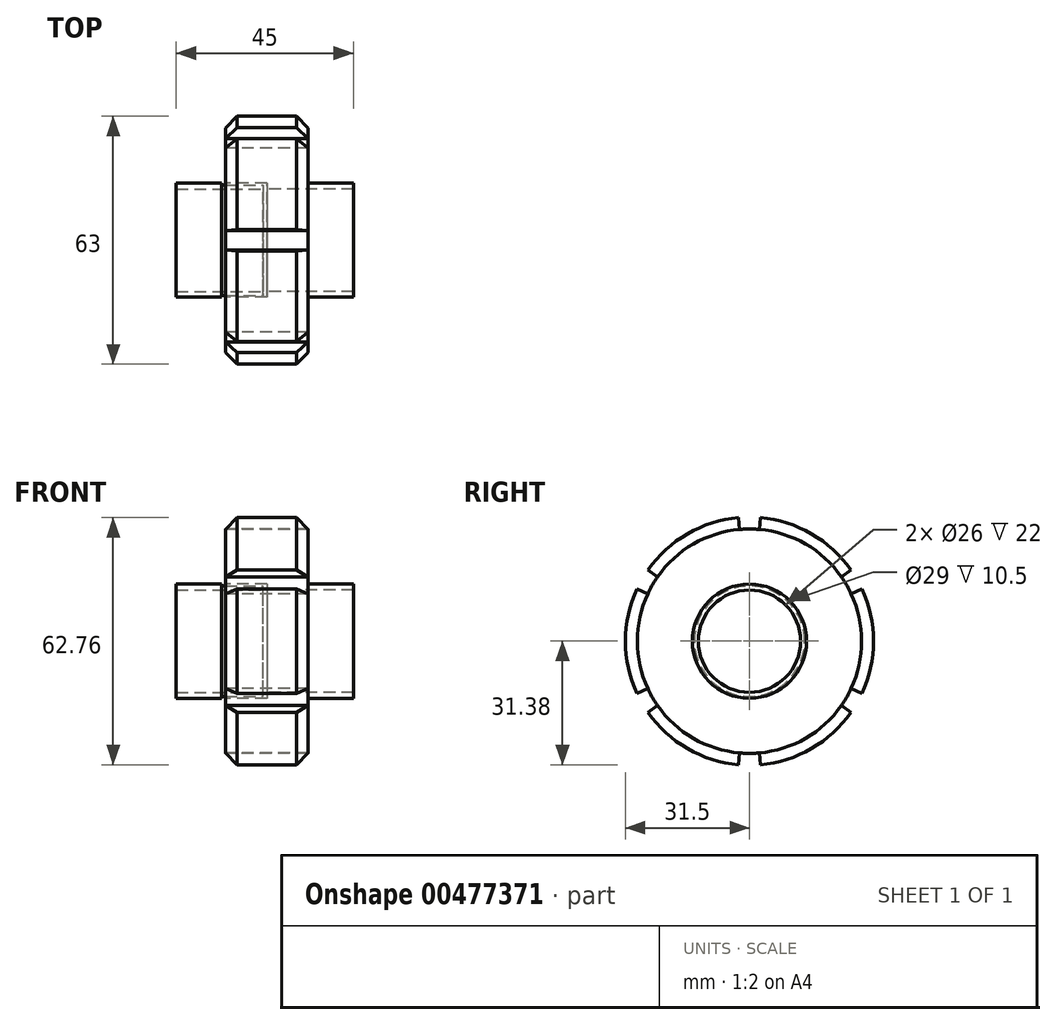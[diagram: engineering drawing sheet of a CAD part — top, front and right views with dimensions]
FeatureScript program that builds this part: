
annotation { "Feature Type Name" : "Feature", "Feature Type Description" : "" }
export const myFeature = defineFeature(function(context is Context, id is Id, definition is map)
    precondition{}
    {
        {
            var Q0;
            Q0=qCreatedBy(makeId("Front.planeOp"),FACE);
            var sketch = newSketch(context, id + "F0", { "sketchPlane" : qUnion([Q0])});
            skLineSegment(sketch, "E0", {"start": v(0, 0) * mm, "end": v(45.26, 0) * mm, "construction": true});
            skLineSegment(sketch, "E1", {"start": v(0, 14.5) * mm, "end": v(0, 31.5) * mm});
            skLineSegment(sketch, "E2", {"start": v(0, 31.5) * mm, "end": v(21, 31.5) * mm});
            skLineSegment(sketch, "E3", {"start": v(21, 31.5) * mm, "end": v(21, 14.5) * mm});
            skLineSegment(sketch, "E4", {"start": v(21, 14.5) * mm, "end": v(32.5, 14.5) * mm});
            skLineSegment(sketch, "E5", {"start": v(32.5, 14.5) * mm, "end": v(32.5, 13) * mm});
            skLineSegment(sketch, "E6", {"start": v(32.5, 13) * mm, "end": v(10.5, 13) * mm});
            skLineSegment(sketch, "E7", {"start": v(10.5, 13) * mm, "end": v(10.5, 14.5) * mm});
            skLineSegment(sketch, "E8", {"start": v(10.5, 14.5) * mm, "end": v(0, 14.5) * mm});
            skSolve(sketch);
        }
        {
            var Q0;
            Q0 = qSketchRegion(id + "F0", true);
            var Q1;
            Q1=sQuery(id+"F0.wireOp",EDGE,"E0");
            revolve(context, id + "F1", {"entities" : qUnion([Q0]), "axis" : qUnion([Q1]), "revolveType" : RevolveType.FULL});
        }
        {
            var Q0;
            Q0=makeQuery(id+"F1.opRevolve","SWEPT_EDGE",EDGE,{"disambiguationData":[OSD([sQuery(id+"F0.wireOp",EDGE,"E1"),sQuery(id+"F0.wireOp",EDGE,"E2")])]});
            var Q1;
            Q1=makeQuery(id+"F1.opRevolve","SWEPT_EDGE",EDGE,{"disambiguationData":[OSD([sQuery(id+"F0.wireOp",EDGE,"E2"),sQuery(id+"F0.wireOp",EDGE,"E3")])]});
            chamfer(context, id + "F2", {"entities" : qUnion([Q0, Q1]), "width" : 3 * mm, "tangentPropagation" : true});
        }
        {
            var Q0;
            Q0=makeQuery(id+"F1.opRevolve","SWEPT_FACE",FACE,{"disambiguationData":[OSD([sQuery(id+"F0.wireOp",EDGE,"E1")])]});
            var sketch = newSketch(context, id + "F3", { "sketchPlane" : qUnion([Q0])});
            skArc(sketch, "E9.0", {"start": v(2.75, 31.38) * mm, "mid": v(0, 31.5) * mm, "end": v(-2.75, 31.38) * mm});
            skArc(sketch, "E10.0", {"start": v(2.48, 28.4) * mm, "mid": v(0, 28.5) * mm, "end": v(-2.48, 28.4) * mm});
            skLineSegment(sketch, "E11", {"start": v(2.48, 28.4) * mm, "end": v(2.75, 31.38) * mm});
            skLineSegment(sketch, "E12", {"start": v(0, 0) * mm, "end": v(0, 19.57) * mm, "construction": true});
            skLineSegment(sketch, "E13.MirrorCS", {"start": v(-2.48, 28.4) * mm, "end": v(-2.75, 31.38) * mm});
            skArc(sketch, "E14.1.0", {"start": v(-23.35, 16.35) * mm, "mid": v(-24.68, 14.25) * mm, "end": v(-25.83, 12.04) * mm});
            skLineSegment(sketch, "E14.1.1", {"start": v(-25.83, 12.04) * mm, "end": v(-28.55, 13.31) * mm});
            skLineSegment(sketch, "E14.1.2", {"start": v(-23.35, 16.35) * mm, "end": v(-25.8, 18.07) * mm});
            skArc(sketch, "E14.1.3", {"start": v(-25.8, 18.07) * mm, "mid": v(-27.28, 15.75) * mm, "end": v(-28.55, 13.31) * mm});
            skArc(sketch, "E14.2.0", {"start": v(-25.83, -12.04) * mm, "mid": v(-24.68, -14.25) * mm, "end": v(-23.35, -16.35) * mm});
            skLineSegment(sketch, "E14.2.1", {"start": v(-23.35, -16.35) * mm, "end": v(-25.8, -18.07) * mm});
            skLineSegment(sketch, "E14.2.2", {"start": v(-25.83, -12.04) * mm, "end": v(-28.55, -13.31) * mm});
            skArc(sketch, "E14.2.3", {"start": v(-28.55, -13.31) * mm, "mid": v(-27.28, -15.75) * mm, "end": v(-25.8, -18.07) * mm});
            skArc(sketch, "E14.3.0", {"start": v(-2.48, -28.4) * mm, "mid": v(0, -28.5) * mm, "end": v(2.48, -28.4) * mm});
            skLineSegment(sketch, "E14.3.1", {"start": v(2.48, -28.4) * mm, "end": v(2.75, -31.38) * mm});
            skLineSegment(sketch, "E14.3.2", {"start": v(-2.48, -28.4) * mm, "end": v(-2.75, -31.38) * mm});
            skArc(sketch, "E14.3.3", {"start": v(-2.75, -31.38) * mm, "mid": v(0, -31.5) * mm, "end": v(2.75, -31.38) * mm});
            skArc(sketch, "E14.4.0", {"start": v(23.35, -16.35) * mm, "mid": v(24.68, -14.25) * mm, "end": v(25.83, -12.04) * mm});
            skLineSegment(sketch, "E14.4.1", {"start": v(25.83, -12.04) * mm, "end": v(28.55, -13.31) * mm});
            skLineSegment(sketch, "E14.4.2", {"start": v(23.35, -16.35) * mm, "end": v(25.8, -18.07) * mm});
            skArc(sketch, "E14.4.3", {"start": v(25.8, -18.07) * mm, "mid": v(27.28, -15.75) * mm, "end": v(28.55, -13.31) * mm});
            skArc(sketch, "E14.5.0", {"start": v(25.83, 12.04) * mm, "mid": v(24.68, 14.25) * mm, "end": v(23.35, 16.35) * mm});
            skLineSegment(sketch, "E14.5.1", {"start": v(23.35, 16.35) * mm, "end": v(25.8, 18.07) * mm});
            skLineSegment(sketch, "E14.5.2", {"start": v(25.83, 12.04) * mm, "end": v(28.55, 13.31) * mm});
            skArc(sketch, "E14.5.3", {"start": v(28.55, 13.31) * mm, "mid": v(27.28, 15.75) * mm, "end": v(25.8, 18.07) * mm});
            skSolve(sketch);
        }
        {
            var Q0;
            Q0 = qSketchRegion(id + "F3", true);
            extrude(context, id + "F4", {"entities" : qUnion([Q0]), "operationType" : NewBodyOperationType.REMOVE, "oppositeDirection" : true, "depth" : 25 * mm});
        }
        {
            var Q0;
            Q0=qCreatedBy(makeId("Front.planeOp"),FACE);
            var sketch = newSketch(context, id + "F5", { "sketchPlane" : qUnion([Q0])});
            skLineSegment(sketch, "E15", {"start": v(-12.5, 14.5) * mm, "end": v(-1, 14.5) * mm});
            skLineSegment(sketch, "E16", {"start": v(9.5, 14) * mm, "end": v(9.5, 13) * mm});
            skLineSegment(sketch, "E17", {"start": v(9.5, 13) * mm, "end": v(-12.5, 13) * mm});
            skLineSegment(sketch, "E18", {"start": v(-12.5, 13) * mm, "end": v(-12.5, 14.5) * mm});
            skLineSegment(sketch, "E19", {"start": v(-1, 14.5) * mm, "end": v(-1, 14) * mm});
            skLineSegment(sketch, "E20", {"start": v(-1, 14) * mm, "end": v(9.5, 14) * mm});
            skLineSegment(sketch, "E21", {"start": v(0, 0) * mm, "end": v(-16.63, 0) * mm, "construction": true});
            skSolve(sketch);
        }
        {
            var Q0;
            Q0 = qSketchRegion(id + "F5", true);
            var Q1;
            Q1=sQuery(id+"F5.wireOp",EDGE,"E21");
            revolve(context, id + "F6", {"entities" : qUnion([Q0]), "axis" : qUnion([Q1]), "revolveType" : RevolveType.FULL});
        }
    });
